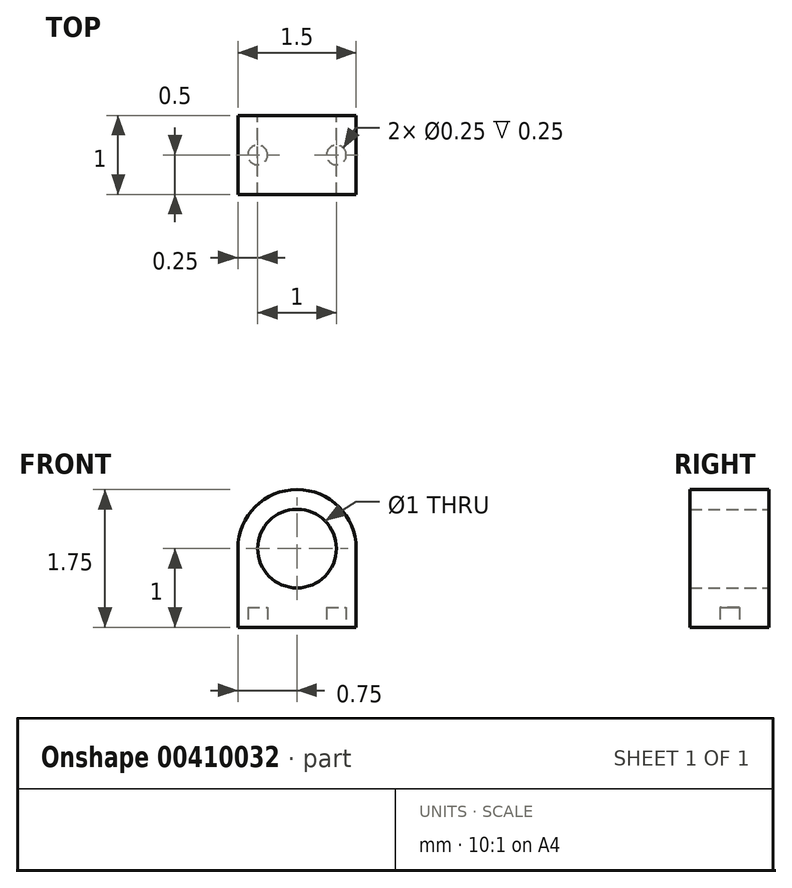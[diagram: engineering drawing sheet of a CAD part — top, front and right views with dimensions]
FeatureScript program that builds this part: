
annotation { "Feature Type Name" : "Feature", "Feature Type Description" : "" }
export const myFeature = defineFeature(function(context is Context, id is Id, definition is map)
    precondition{}
    {
        {
            var Q0;
            Q0=qCreatedBy(makeId("Front.planeOp"),FACE);
            var sketch = newSketch(context, id + "F0", { "sketchPlane" : qUnion([Q0])});
            skLineSegment(sketch, "E0.bottom", {"start": v(0, 0) * mm, "end": v(1.5, 0) * mm});
            skLineSegment(sketch, "E0.top", {"start": v(0, 1) * mm, "end": v(1.5, 1) * mm});
            skLineSegment(sketch, "E0.left", {"start": v(0, 0) * mm, "end": v(0, 1) * mm});
            skLineSegment(sketch, "E0.right", {"start": v(1.5, 0) * mm, "end": v(1.5, 1) * mm});
            skCircle(sketch, "E1", {"center": v(0.75, 1) * mm, "radius": 0.75 * mm});
            skCircle(sketch, "E2", {"center": v(0.75, 1) * mm, "radius": 0.5 * mm});
            skSolve(sketch);
        }
        {
            var Q0;
            Q0=makeQuery(id+"F0.imprint","IMPRINT",FACE,{"disambiguationData":[TD([[makeQuery(id+"F0.imprint","IMPRINT",EDGE,{"derivedFrom":sQuery(id+"F0.wireOp",EDGE,"E0.bottom")}),1.0]])]});
            var Q1;
            {var subQ1=sQuery(id+"F0.wireOp",EDGE,"E0.top");var subQ3=sQuery(id+"F0.wireOp",EDGE,"E2");var subQ4=makeQuery(id+"F0.imprint","INTERSECT",VERTEX,{"disambiguationData":[OD(0.0)],"derivedFrom":[subQ1,subQ3]});Q1=makeQuery(id+"F0.imprint","IMPRINT",FACE,{"disambiguationData":[TD([[makeQuery(id+"F0.imprint","IMPRINT",EDGE,{"disambiguationData":[TD([[subQ4,-1.0]])],"derivedFrom":subQ3}),-1.0]])]});}
            var Q2;
            {var subQ1=sQuery(id+"F0.wireOp",EDGE,"E0.top");var subQ3=sQuery(id+"F0.wireOp",EDGE,"E2");var subQ4=makeQuery(id+"F0.imprint","INTERSECT",VERTEX,{"disambiguationData":[OD(0.0)],"derivedFrom":[subQ1,subQ3]});Q2=makeQuery(id+"F0.imprint","IMPRINT",FACE,{"disambiguationData":[TD([[makeQuery(id+"F0.imprint","IMPRINT",EDGE,{"disambiguationData":[TD([[subQ4,1.0]])],"derivedFrom":subQ3}),-1.0]])]});}
            extrude(context, id + "F1", {"entities" : qUnion([Q0, Q1, Q2]), "depth" : 1 * mm});
        }
        {
            var Q0;
            Q0=makeQuery(id+"F1.opExtrude","SWEPT_FACE",FACE,{"disambiguationData":[OSD([sQuery(id+"F0.wireOp",EDGE,"E0.bottom")])]});
            var sketch = newSketch(context, id + "F2", { "sketchPlane" : qUnion([Q0])});
            skCircle(sketch, "E3", {"center": v(1.25, 0.5) * mm, "radius": 0.12 * mm});
            skPoint(sketch, "E3.centerSnap0", {"position": v(1.5, 0.5) * mm});
            skCircle(sketch, "E4", {"center": v(0.25, 0.5) * mm, "radius": 0.12 * mm});
            skSolve(sketch);
        }
        {
            var Q0;
            Q0 = qSketchRegion(id + "F2", true);
            extrude(context, id + "F3", {"entities" : qUnion([Q0]), "operationType" : NewBodyOperationType.REMOVE, "oppositeDirection" : true, "depth" : 0.25 * mm});
        }
    });
